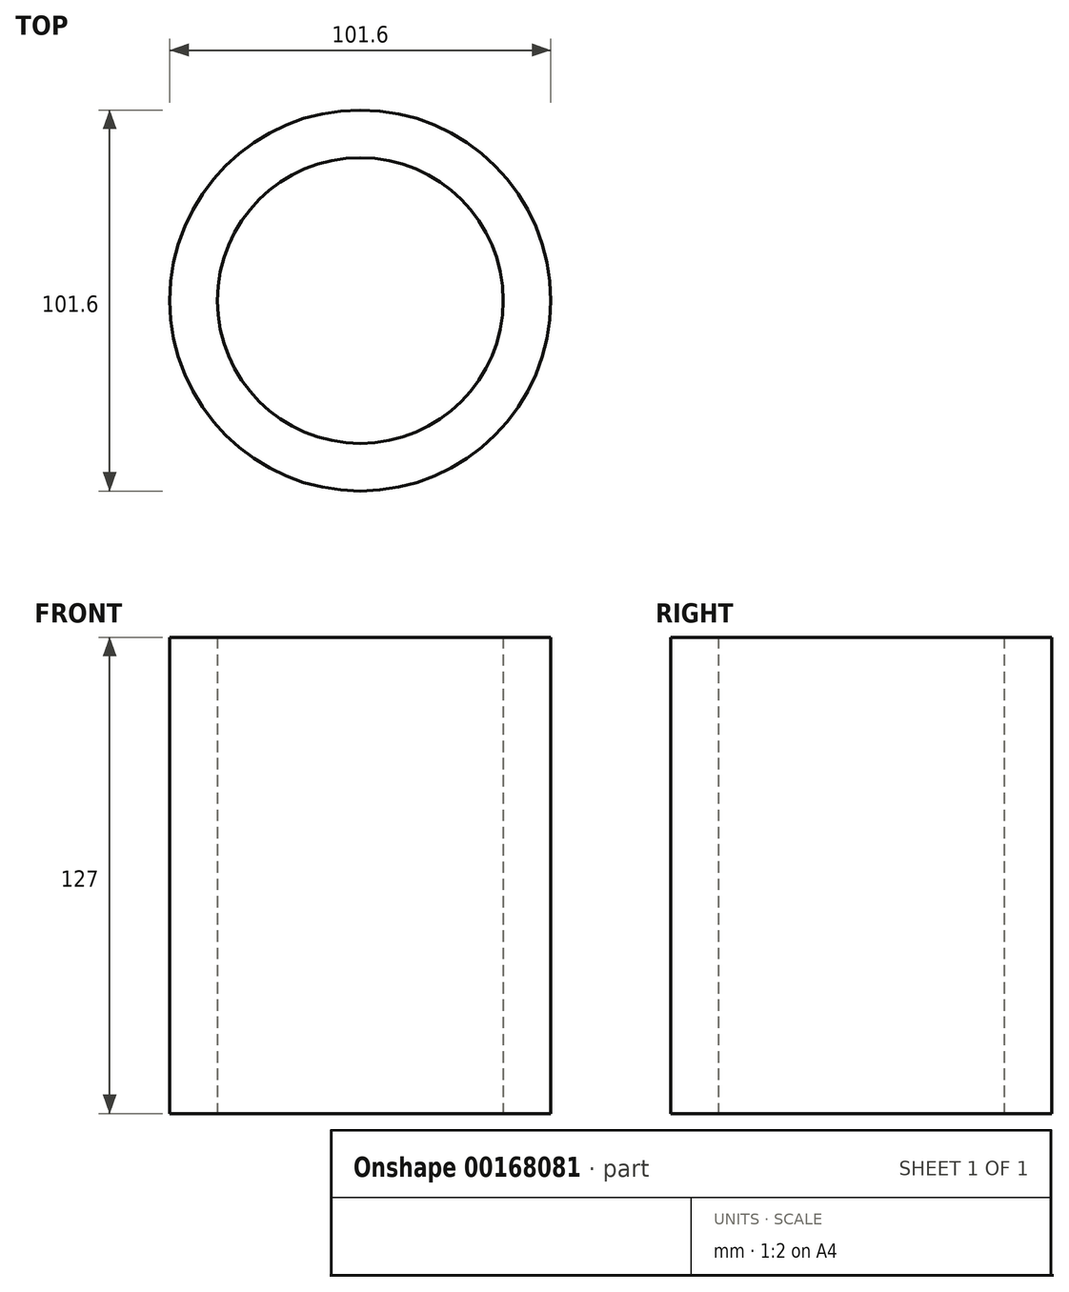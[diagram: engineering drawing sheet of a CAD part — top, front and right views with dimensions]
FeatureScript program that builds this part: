
annotation { "Feature Type Name" : "Feature", "Feature Type Description" : "" }
export const myFeature = defineFeature(function(context is Context, id is Id, definition is map)
    precondition{}
    {
        {
            var Q0;
            Q0=qCreatedBy(makeId("Top.planeOp"),FACE);
            var sketch = newSketch(context, id + "F0", { "sketchPlane" : qUnion([Q0])});
            skCircle(sketch, "E0", {"center": v(0, 0) * mm, "radius": 38.1 * mm});
            skCircle(sketch, "E1", {"center": v(0, 0) * mm, "radius": 50.8 * mm});
            skSolve(sketch);
        }
        {
            var Q0;
            Q0 = qSketchRegion(id + "F0", true);
            extrude(context, id + "F1", {"entities" : qUnion([Q0]), "depth" : 127 * mm});
        }
    });
